# Revit family: Centralini_in_lamiera_Bticino_da_parete_porta_piena
name_source: partatom
category: Equipement électrique
revit_build: Autodesk Revit 2018 (Build: 20170223_1515(x64)
units: mm (PartAtom-declared; Revit-internal decimal feet)

## family parameters
Basée sur le plan de construction = Non
Configuration du panneau = Deux colonnes, circuits au sein
Cote de connecteur circulaire = Utiliser le diamètre
Couper avec des vides une fois chargée = Non
Numéro OmniClass = 23.80.30.11.17
Partagée = Non
Point de calcul de pièce = Non
Titre OmniClass = Distribution Boards and Control Panels
Toujours verticalement = Oui
Type d'élément = Tableau de raccordement

## types (6) — shared parameters
Colore = RAL 7035
Condizioni Generali di Utilizzo = https://export.legrand.com
Fabricant = bticino
IK = 08
IP = 30
URL = www.bticino.com
materia = metallo

## per-type parameters (varying)
| type | E109P/12D | E109P/24D | E109P/36D | E109P/54D | E109P/72D | E109P/96D | altezza | larghezza | profondità |
| Centralini per terziaro Bticino E109P/12D | Oui | Non | Non | Non | Non | Non | 300 mm | 300 mm | 90 mm  [stored 0.295276 ft] |
| Centralini per terziaro Bticino E109P/24D | Non | Oui | Non | Non | Non | Non | 425 mm  [stored 1.39436 ft] | 300 mm | 90 mm  [stored 0.295276 ft] |
| Centralini per terziaro Bticino E109P/36D | Non | Non | Oui | Non | Non | Non | 550 mm | 300 mm | 90 mm  [stored 0.295276 ft] |
| Centralini per terziaro Bticino E109P/54D | Non | Non | Non | Oui | Non | Non | 680 mm  [stored 2.23097 ft] | 470 mm  [stored 1.54199 ft] | 120 mm  [stored 0.393701 ft] |
| Centralini per terziaro Bticino E109P/72D | Non | Non | Non | Non | Oui | Non | 680 mm  [stored 2.23097 ft] | 630 mm  [stored 2.06693 ft] | 120 mm  [stored 0.393701 ft] |
| Centralini per terziaro Bticino E109P/96D | Non | Non | Non | Non | Non | Oui | 830 mm  [stored 2.7231 ft] | 630 mm  [stored 2.06693 ft] | 120 mm  [stored 0.393701 ft] |

note: [stored X ft] marks values corroborated as IEEE doubles in the binary element streams (Revit-internal decimal feet)
